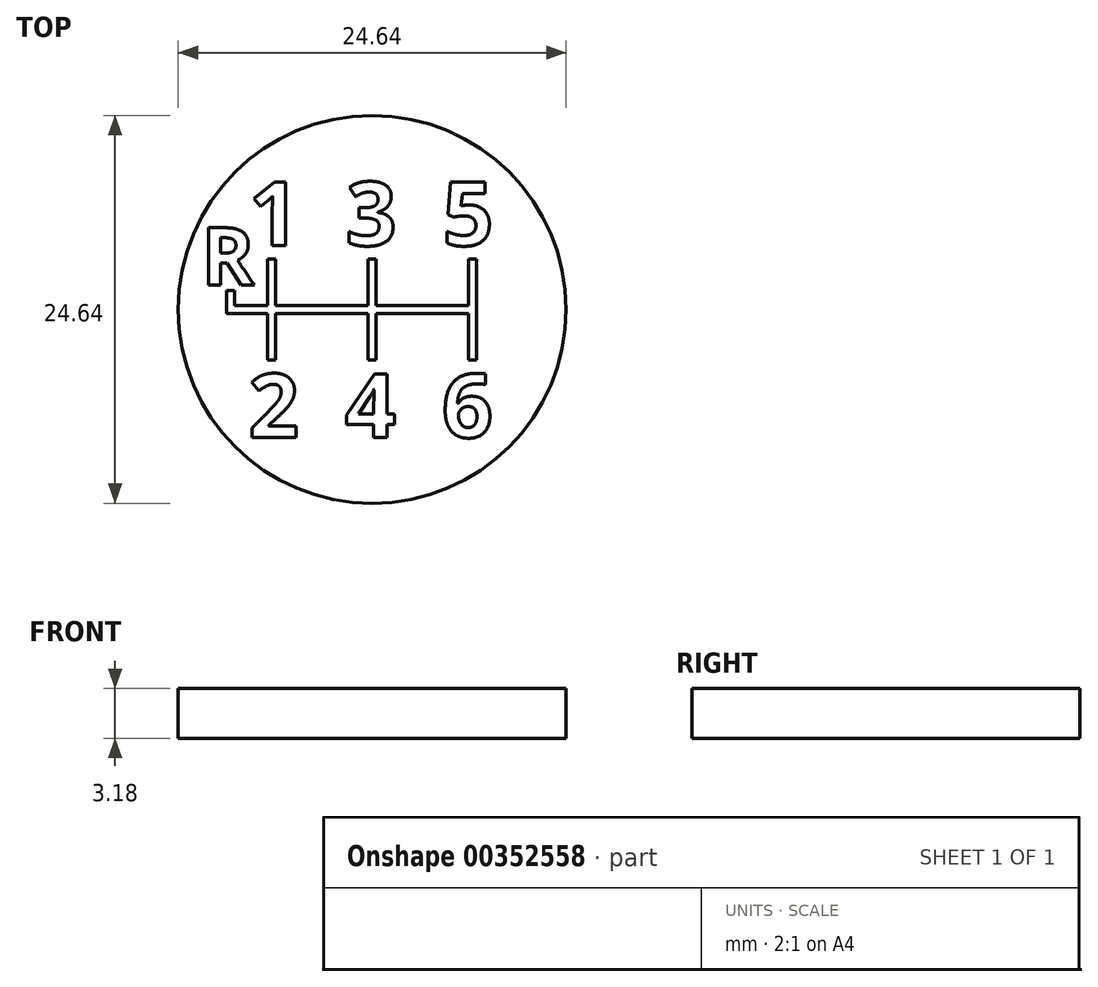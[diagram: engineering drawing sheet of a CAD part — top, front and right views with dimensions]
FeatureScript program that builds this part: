
annotation { "Feature Type Name" : "Feature", "Feature Type Description" : "" }
export const myFeature = defineFeature(function(context is Context, id is Id, definition is map)
    precondition{}
    {
        {
            var Q0;
            Q0=qCreatedBy(makeId("Top.planeOp"),FACE);
            var sketch = newSketch(context, id + "F0", { "sketchPlane" : qUnion([Q0])});
            skCircle(sketch, "E0", {"center": v(0, 0) * mm, "radius": 12.32 * mm});
            skSolve(sketch);
        }
        {
            var Q0;
            Q0 = qSketchRegion(id + "F0", true);
            extrude(context, id + "F1", {"entities" : qUnion([Q0]), "depth" : 3.17 * mm});
        }
        {
            var Q0;
            Q0=makeQuery(id+"F1.opExtrude","CAP_FACE",FACE,{"disambiguationData":[OSD([sQuery(id+"F0.wireOp",EDGE,"E0")])],"isStart":false});
            var sketch = newSketch(context, id + "F2", { "sketchPlane" : qUnion([Q0])});
            skText(sketch, "E1", { "text": "R", "fontName": "OpenSans-Bold.ttf"});
            skText(sketch, "E2", { "text": "1  3  5\n", "fontName": "OpenSans-Bold.ttf"});
            skText(sketch, "E3", { "text": "2  4  6", "fontName": "OpenSans-Bold.ttf"});
            skLineSegment(sketch, "E4.bottom", {"start": v(0, 4.06) * mm, "end": v(0, 4.06) * mm});
            skLineSegment(sketch, "E4.top", {"start": v(0, -4.06) * mm, "end": v(0, -4.06) * mm});
            skLineSegment(sketch, "E5.bottom", {"start": v(6.12, 0.25) * mm, "end": v(0.25, 0.25) * mm});
            skLineSegment(sketch, "E5.top", {"start": v(6.12, -0.25) * mm, "end": v(0.25, -0.25) * mm});
            skPoint(sketch, "E5.middle", {"position": v(0, 0) * mm});
            skLineSegment(sketch, "E6.bottom", {"start": v(0.25, 3.2) * mm, "end": v(-0.25, 3.2) * mm});
            skLineSegment(sketch, "E6.top", {"start": v(0.25, -3.2) * mm, "end": v(-0.25, -3.2) * mm});
            skLineSegment(sketch, "E6.left", {"start": v(0.25, 3.2) * mm, "end": v(0.25, 0.25) * mm});
            skLineSegment(sketch, "E6.right", {"start": v(-0.25, 3.2) * mm, "end": v(-0.25, 0.25) * mm});
            skLineSegment(sketch, "E7.bottom", {"start": v(6.63, 3.2) * mm, "end": v(6.12, 3.2) * mm});
            skLineSegment(sketch, "E7.top", {"start": v(6.63, -3.2) * mm, "end": v(6.12, -3.2) * mm});
            skLineSegment(sketch, "E7.left", {"start": v(6.63, 3.2) * mm, "end": v(6.63, -3.2) * mm});
            skLineSegment(sketch, "E7.right", {"start": v(6.12, 3.2) * mm, "end": v(6.12, 0.25) * mm});
            skLineSegment(sketch, "E8.bottom", {"start": v(-6.12, 3.2) * mm, "end": v(-6.63, 3.2) * mm});
            skLineSegment(sketch, "E8.top", {"start": v(-6.12, -3.2) * mm, "end": v(-6.63, -3.2) * mm});
            skLineSegment(sketch, "E8.left", {"start": v(-6.12, 3.2) * mm, "end": v(-6.12, 0.25) * mm});
            skLineSegment(sketch, "E8.right", {"start": v(-6.63, 3.2) * mm, "end": v(-6.63, 0.25) * mm});
            skPoint(sketch, "E9.middle", {"position": v(0.25, 3.2) * mm});
            skLineSegment(sketch, "E10.top", {"start": v(-9, -0.25) * mm, "end": v(-6.63, -0.25) * mm});
            skLineSegment(sketch, "E11.bottom", {"start": v(-8.74, 1.2) * mm, "end": v(-9.25, 1.2) * mm});
            skLineSegment(sketch, "E11.left", {"start": v(-8.74, 1.2) * mm, "end": v(-8.74, 0.25) * mm});
            skLineSegment(sketch, "E11.right", {"start": v(-9.25, 1.2) * mm, "end": v(-9.25, -0.25) * mm});
            skPoint(sketch, "E11.middle", {"position": v(-9, 0) * mm});
            skLineSegment(sketch, "E12", {"start": v(-6.63, 0.25) * mm, "end": v(-8.74, 0.25) * mm});
            skLineSegment(sketch, "E13", {"start": v(-9, -0.25) * mm, "end": v(-9.25, -0.25) * mm});
            skPoint(sketch, "E13.endSnap0", {"position": v(-9.25, 0) * mm});
            skLineSegment(sketch, "E14.trimOffspring", {"start": v(-6.12, -0.25) * mm, "end": v(-6.12, -3.2) * mm});
            skLineSegment(sketch, "E15.trimOffspring", {"start": v(-6.63, -0.25) * mm, "end": v(-6.63, -3.2) * mm});
            skLineSegment(sketch, "E16.trimOffspring", {"start": v(-0.25, 0.25) * mm, "end": v(-6.12, 0.25) * mm});
            skLineSegment(sketch, "E17.trimOffspring", {"start": v(0.25, -0.25) * mm, "end": v(0.25, -3.2) * mm});
            skLineSegment(sketch, "E18.trimOffspring", {"start": v(-0.25, -0.25) * mm, "end": v(-6.12, -0.25) * mm});
            skLineSegment(sketch, "E19.trimOffspring", {"start": v(-0.25, -0.25) * mm, "end": v(-0.25, -3.2) * mm});
            skLineSegment(sketch, "E20.trimOffspring", {"start": v(6.12, -0.25) * mm, "end": v(6.12, -3.2) * mm});
            const initialGuessF2  = {"E1": [-0.01085, 0.00154, 1, 0, 0.00368], "E2": [-0.00782, 0.00406, 1, 0, 0.00406], "E3": [-0.00786, -0.00813, 1, 0, 0.00406]};
            skSetInitialGuess(sketch, initialGuessF2);
            skSolve(sketch);
        }
        {
            var Q0;
            Q0 = qSketchRegion(id + "F2", true);
            extrude(context, id + "F3", {"entities" : qUnion([Q0]), "operationType" : NewBodyOperationType.REMOVE, "oppositeDirection" : true, "depth" : 1 / 406.4 * mm});
        }
    });
